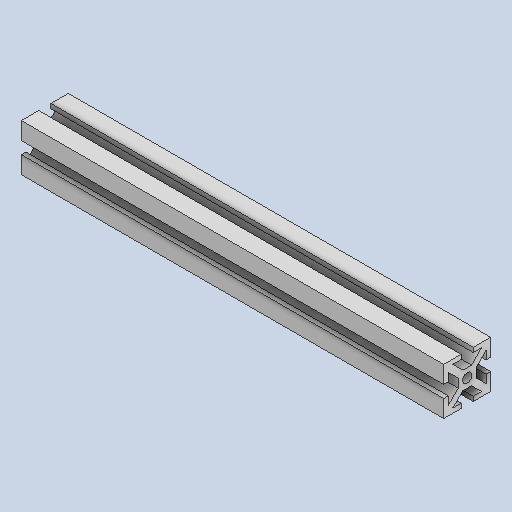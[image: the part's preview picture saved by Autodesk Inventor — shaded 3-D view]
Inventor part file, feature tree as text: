
AUTODESK INVENTOR PART (.ipt)
format: ipt  version: 2023 (Build 270158030, 158C)  size: 155,136 bytes
history: native  units: in
note: dims shown in document units (in); Inventor stores cm internally (conversion verified against a paired STEP export)
features: extrude x1, sketch x1
ambient origin geometry x8: Origin, YZ Plane, XZ Plane, XY Plane, X Axis, Y Axis, Z Axis, Center Point
bodies: Solid1 (feature_tree)
feature tree (2):
  extrude  "Extrusion1"  Depth=0.0975in
  sketch  "Sketch1"  dims[d2=0.37in d3=0.0975in d7=0.0975in d10=0.0975in d11=1.0in d13=0.0975in d16=0.0975in d17=0.37in d18=1.0in d23=0.0975in d24=1.0in d25=1.0in d32=0.175in d33=0.175in d35=135.0deg d36=0.175in d37=0.175in d38=0.0975in d40=0.175in d41=0.175in d42=0.175in d43=0.175in d44=0.2in d45=9.0in d46=0.0in]
